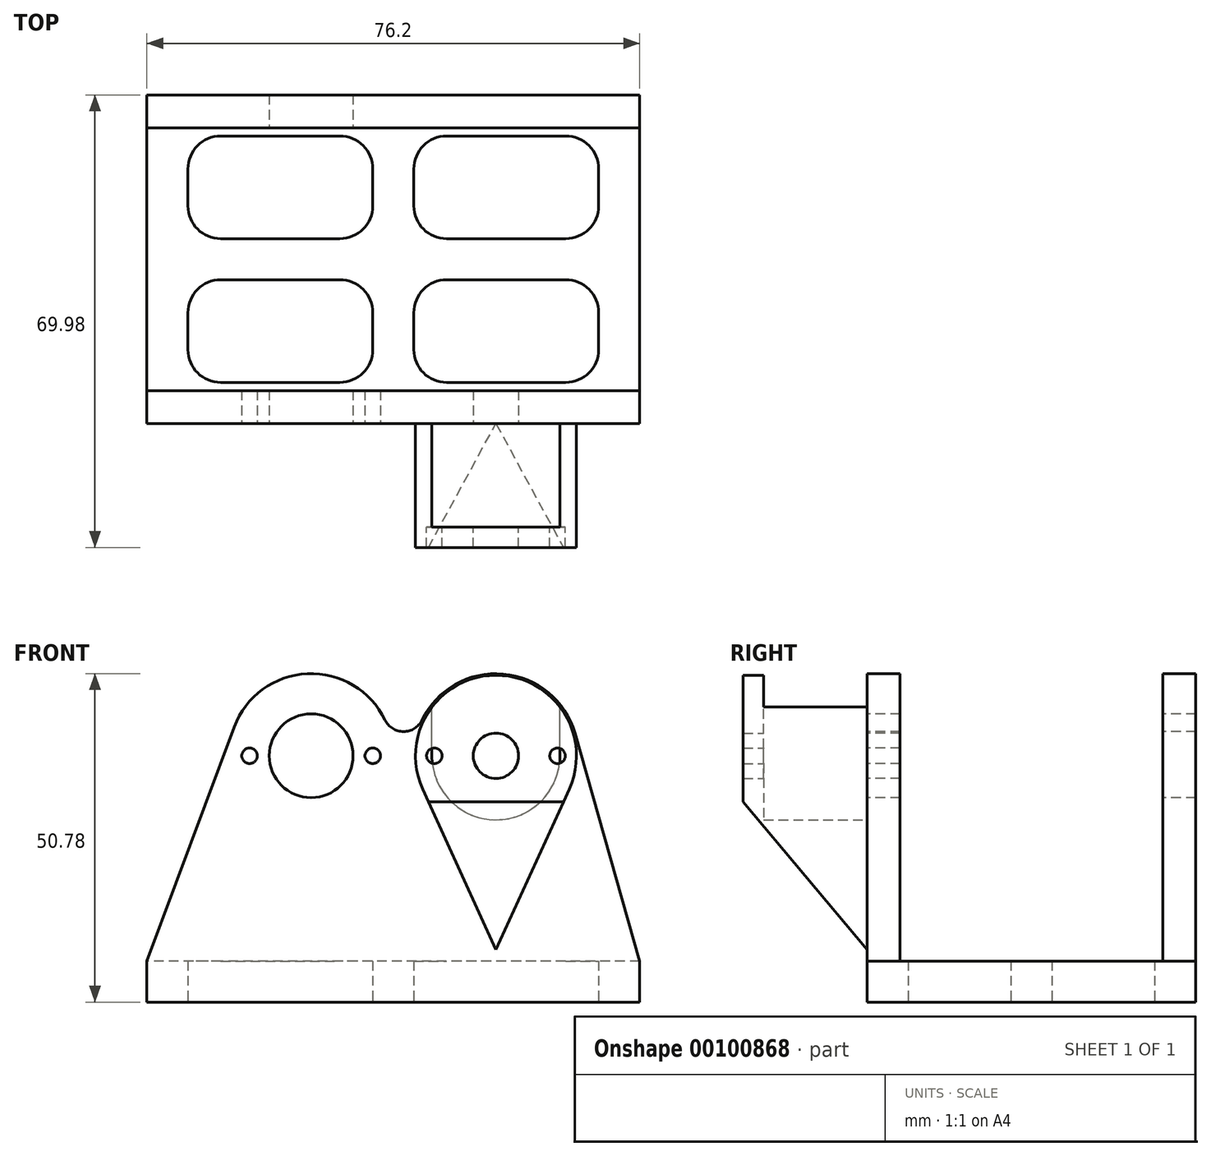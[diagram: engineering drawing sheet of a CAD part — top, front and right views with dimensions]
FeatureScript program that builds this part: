
annotation { "Feature Type Name" : "Feature", "Feature Type Description" : "" }
export const myFeature = defineFeature(function(context is Context, id is Id, definition is map)
    precondition{}
    {
        {
            var Q0;
            Q0=qCreatedBy(makeId("Top.planeOp"),FACE);
            var sketch = newSketch(context, id + "F0", { "sketchPlane" : qUnion([Q0])});
            skLineSegment(sketch, "E0.bottom", {"start": v(38.1, -25.4) * mm, "end": v(-38.1, -25.4) * mm});
            skLineSegment(sketch, "E0.top", {"start": v(38.1, 25.4) * mm, "end": v(-38.1, 25.4) * mm});
            skLineSegment(sketch, "E0.left", {"start": v(38.1, -25.4) * mm, "end": v(38.1, 25.4) * mm});
            skLineSegment(sketch, "E0.right", {"start": v(-38.1, -25.4) * mm, "end": v(-38.1, 25.4) * mm});
            skPoint(sketch, "E0.middle", {"position": v(0, 0) * mm});
            skLineSegment(sketch, "E1", {"start": v(0, 0) * mm, "end": v(12.76, 0) * mm, "construction": true});
            skLineSegment(sketch, "E2", {"start": v(0, 0) * mm, "end": v(0, 25.4) * mm, "construction": true});
            skLineSegment(sketch, "E3.MirrorCS", {"start": v(0, 0) * mm, "end": v(0, -25.4) * mm, "construction": true});
            skLineSegment(sketch, "E4.bottom", {"start": v(-26.67, 19.05) * mm, "end": v(-8.26, 19.05) * mm});
            skLineSegment(sketch, "E4.top", {"start": v(-26.67, 3.17) * mm, "end": v(-8.26, 3.17) * mm});
            skLineSegment(sketch, "E4.left", {"start": v(-31.75, 13.97) * mm, "end": v(-31.75, 8.25) * mm});
            skLineSegment(sketch, "E4.right", {"start": v(-3.18, 13.97) * mm, "end": v(-3.18, 8.25) * mm});
            skPoint(sketch, "E4.middle", {"position": v(-17.46, 11.11) * mm});
            skPoint(sketch, "E5.visualSharp", {"position": v(-31.75, 3.17) * mm});
            skArc(sketch, "E5.filletArc", {"start": v(-31.75, 8.25) * mm, "mid": v(-30.26, 4.66) * mm, "end": v(-26.67, 3.17) * mm});
            skPoint(sketch, "E6.visualSharp", {"position": v(-31.75, 19.05) * mm});
            skArc(sketch, "E6.filletArc", {"start": v(-26.67, 19.05) * mm, "mid": v(-30.26, 17.56) * mm, "end": v(-31.75, 13.97) * mm});
            skPoint(sketch, "E7.visualSharp", {"position": v(-3.18, 19.05) * mm});
            skArc(sketch, "E7.filletArc", {"start": v(-3.18, 13.97) * mm, "mid": v(-4.66, 17.56) * mm, "end": v(-8.26, 19.05) * mm});
            skPoint(sketch, "E8.visualSharp", {"position": v(-3.18, 3.17) * mm});
            skArc(sketch, "E8.filletArc", {"start": v(-8.26, 3.17) * mm, "mid": v(-4.66, 4.66) * mm, "end": v(-3.18, 8.25) * mm});
            skArc(sketch, "E9.MirrorCS", {"start": v(31.75, 8.26) * mm, "mid": v(30.26, 4.66) * mm, "end": v(26.67, 3.18) * mm});
            skLineSegment(sketch, "E10.MirrorCS", {"start": v(31.75, 13.97) * mm, "end": v(31.75, 8.26) * mm});
            skArc(sketch, "E11.MirrorCS", {"start": v(26.67, 19.05) * mm, "mid": v(30.26, 17.56) * mm, "end": v(31.75, 13.97) * mm});
            skLineSegment(sketch, "E12.MirrorCS", {"start": v(26.67, 19.05) * mm, "end": v(8.25, 19.05) * mm});
            skArc(sketch, "E13.MirrorCS", {"start": v(3.17, 13.97) * mm, "mid": v(4.66, 17.56) * mm, "end": v(8.25, 19.05) * mm});
            skLineSegment(sketch, "E14.MirrorCS", {"start": v(3.17, 13.97) * mm, "end": v(3.17, 8.25) * mm});
            skArc(sketch, "E15.MirrorCS", {"start": v(8.26, 3.18) * mm, "mid": v(4.66, 4.66) * mm, "end": v(3.17, 8.25) * mm});
            skLineSegment(sketch, "E16.MirrorCS", {"start": v(26.67, 3.18) * mm, "end": v(8.26, 3.17) * mm});
            skLineSegment(sketch, "E17.MirrorCS", {"start": v(-26.67, -3.18) * mm, "end": v(-8.26, -3.18) * mm});
            skArc(sketch, "E18.MirrorCS", {"start": v(-31.75, -8.26) * mm, "mid": v(-30.26, -4.66) * mm, "end": v(-26.67, -3.18) * mm});
            skLineSegment(sketch, "E19.MirrorCS", {"start": v(-31.75, -13.97) * mm, "end": v(-31.75, -8.26) * mm});
            skArc(sketch, "E20.MirrorCS", {"start": v(-26.67, -19.05) * mm, "mid": v(-30.26, -17.56) * mm, "end": v(-31.75, -13.97) * mm});
            skLineSegment(sketch, "E21.MirrorCS", {"start": v(-26.67, -19.05) * mm, "end": v(-8.25, -19.05) * mm});
            skArc(sketch, "E22.MirrorCS", {"start": v(-3.17, -13.97) * mm, "mid": v(-4.66, -17.56) * mm, "end": v(-8.25, -19.05) * mm});
            skLineSegment(sketch, "E23.MirrorCS", {"start": v(-3.17, -13.97) * mm, "end": v(-3.17, -8.26) * mm});
            skPoint(sketch, "E24.MirrorP", {"position": v(-3.17, -3.18) * mm});
            skArc(sketch, "E25.MirrorCS", {"start": v(-8.26, -3.18) * mm, "mid": v(-4.66, -4.66) * mm, "end": v(-3.17, -8.26) * mm});
            skLineSegment(sketch, "E26.MirrorCS", {"start": v(3.18, -13.97) * mm, "end": v(3.18, -8.26) * mm});
            skArc(sketch, "E27.MirrorCS", {"start": v(8.26, -3.17) * mm, "mid": v(4.66, -4.66) * mm, "end": v(3.18, -8.26) * mm});
            skArc(sketch, "E28.MirrorCS", {"start": v(3.18, -13.97) * mm, "mid": v(4.66, -17.56) * mm, "end": v(8.26, -19.05) * mm});
            skLineSegment(sketch, "E29.MirrorCS", {"start": v(26.67, -19.05) * mm, "end": v(8.26, -19.05) * mm});
            skLineSegment(sketch, "E30.MirrorCS", {"start": v(26.67, -3.17) * mm, "end": v(8.26, -3.18) * mm});
            skArc(sketch, "E31.MirrorCS", {"start": v(31.75, -8.26) * mm, "mid": v(30.26, -4.66) * mm, "end": v(26.67, -3.18) * mm});
            skLineSegment(sketch, "E32.MirrorCS", {"start": v(31.75, -13.97) * mm, "end": v(31.75, -8.26) * mm});
            skArc(sketch, "E33.MirrorCS", {"start": v(26.67, -19.05) * mm, "mid": v(30.26, -17.56) * mm, "end": v(31.75, -13.97) * mm});
            skSolve(sketch);
        }
        {
            var Q0;
            Q0 = qSketchRegion(id + "F0", true);
            extrude(context, id + "F1", {"entities" : qUnion([Q0]), "depth" : 6.35 * mm});
        }
        {
            var Q0;
            Q0=makeQuery(id+"F1.opExtrude","CAP_FACE",FACE,{"disambiguationData":[OSD([sQuery(id+"F0.wireOp",EDGE,"E0.bottom"),sQuery(id+"F0.wireOp",EDGE,"E0.top"),sQuery(id+"F0.wireOp",EDGE,"E0.left"),sQuery(id+"F0.wireOp",EDGE,"E0.right")])],"isStart":false});
            var sketch = newSketch(context, id + "F2", { "sketchPlane" : qUnion([Q0])});
            skLineSegment(sketch, "E34.bottom", {"start": v(-38.1, 25.4) * mm, "end": v(38.1, 25.4) * mm});
            skLineSegment(sketch, "E34.top", {"start": v(-38.1, 20.32) * mm, "end": v(38.1, 20.32) * mm});
            skLineSegment(sketch, "E34.left", {"start": v(-38.1, 25.4) * mm, "end": v(-38.1, 20.32) * mm});
            skLineSegment(sketch, "E34.right", {"start": v(38.1, 25.4) * mm, "end": v(38.1, 20.32) * mm});
            skLineSegment(sketch, "E35.bottom", {"start": v(38.1, -25.4) * mm, "end": v(-38.1, -25.4) * mm});
            skLineSegment(sketch, "E35.top", {"start": v(38.1, -20.32) * mm, "end": v(-38.1, -20.32) * mm});
            skLineSegment(sketch, "E35.left", {"start": v(38.1, -25.4) * mm, "end": v(38.1, -20.32) * mm});
            skLineSegment(sketch, "E35.right", {"start": v(-38.1, -25.4) * mm, "end": v(-38.1, -20.32) * mm});
            skSolve(sketch);
        }
        {
            var Q0;
            Q0 = qSketchRegion(id + "F2", true);
            extrude(context, id + "F3", {"entities" : qUnion([Q0]), "operationType" : NewBodyOperationType.ADD, "depth" : 101.6 * mm});
        }
        {
            var Q0;
            Q0=makeQuery(id+"F3.boolean.opBoolean","MERGE",FACE,{"derivedFrom":[makeQuery(id+"F1.opExtrude","SWEPT_FACE",FACE,{"disambiguationData":[OSD([sQuery(id+"F0.wireOp",EDGE,"E0.bottom")])]}),makeQuery(id+"F3.opExtrude","SWEPT_FACE",FACE,{"disambiguationData":[OSD([sQuery(id+"F2.wireOp",EDGE,"E35.bottom")])]})]});
            var sketch = newSketch(context, id + "F4", { "sketchPlane" : qUnion([Q0])});
            skCircle(sketch, "E36", {"center": v(-12.7, 38.08) * mm, "radius": 6.48 * mm});
            skCircle(sketch, "E37", {"center": v(-22.22, 38.08) * mm, "radius": 1.2 * mm});
            skCircle(sketch, "E38", {"center": v(-3.17, 38.08) * mm, "radius": 1.2 * mm});
            skLineSegment(sketch, "E39", {"start": v(-3.17, 38.08) * mm, "end": v(-12.7, 38.08) * mm, "construction": true});
            skLineSegment(sketch, "E40", {"start": v(-12.7, 38.08) * mm, "end": v(-22.22, 38.08) * mm, "construction": true});
            skCircle(sketch, "E41", {"center": v(-12.7, 38.08) * mm, "radius": 28.58 * mm, "construction": true});
            skPoint(sketch, "E42.visualSharp", {"position": v(19.22, 48.59) * mm});
            skPoint(sketch, "E43.visualSharp", {"position": v(-7.63, 23.99) * mm});
            skLineSegment(sketch, "E44", {"start": v(38.1, 6.35) * mm, "end": v(38.1, 107.95) * mm});
            skLineSegment(sketch, "E45", {"start": v(38.1, 107.95) * mm, "end": v(-38.1, 107.95) * mm});
            skLineSegment(sketch, "E46", {"start": v(-38.1, 107.95) * mm, "end": v(-38.1, 6.35) * mm});
            skArc(sketch, "E47", {"start": v(-1.27, 43.62) * mm, "mid": v(-13.3, 50.77) * mm, "end": v(-24.6, 42.52) * mm});
            skLineSegment(sketch, "E48", {"start": v(-38.1, 6.35) * mm, "end": v(-24.6, 42.52) * mm});
            skLineSegment(sketch, "E49", {"start": v(38.1, 6.35) * mm, "end": v(28.1, 41.55) * mm});
            skPoint(sketch, "E50.center.orphan", {"position": v(15.88, 38.08) * mm});
            skPoint(sketch, "E51.visualSharp", {"position": v(-1.27, 32.55) * mm});
            skPoint(sketch, "E52.visualSharp", {"position": v(31.24, 47.34) * mm});
            skPoint(sketch, "E53.visualSharp", {"position": v(-1.27, 43.62) * mm});
            skPoint(sketch, "E54.visualSharp", {"position": v(33.41, 33.23) * mm});
            skCircle(sketch, "E55", {"center": v(15.88, 38.08) * mm, "radius": 3.5 * mm});
            skArc(sketch, "E56", {"start": v(28.1, 41.55) * mm, "mid": v(16.98, 50.73) * mm, "end": v(4.45, 43.62) * mm});
            skArc(sketch, "E57", {"start": v(-1.27, 43.62) * mm, "mid": v(1.59, 41.83) * mm, "end": v(4.45, 43.62) * mm});
            skSolve(sketch);
        }
        {
            var Q0;
            Q0=makeQuery(id+"F4.imprint","IMPRINT",FACE,{"disambiguationData":[TD([[makeQuery(id+"F4.imprint","IMPRINT",EDGE,{"derivedFrom":sQuery(id+"F4.wireOp",EDGE,"E44")}),-1.0]])]});
            var Q1;
            Q1=makeQuery(id+"F4.imprint","IMPRINT",FACE,{"disambiguationData":[TD([[makeQuery(id+"F4.imprint","IMPRINT",EDGE,{"derivedFrom":sQuery(id+"F4.wireOp",EDGE,"VKw5fcWm-w3NF-tdAb-OPDk-Neu4bGwbLTaV")}),1.0]])]});
            var Q2;
            Q2=makeQuery(id+"F4.imprint","IMPRINT",FACE,{"disambiguationData":[TD([[makeQuery(id+"F4.imprint","IMPRINT",EDGE,{"derivedFrom":sQuery(id+"F4.wireOp",EDGE,"E36")}),1.0]])]});
            extrude(context, id + "F5", {"entities" : qUnion([Q0, Q1, Q2]), "operationType" : NewBodyOperationType.REMOVE, "endBound" : BoundingType.THROUGH_ALL, "oppositeDirection" : true, "depth" : 25.4 * mm});
        }
        {
            var Q0;
            Q0=makeQuery(id+"F4.imprint","IMPRINT",FACE,{"disambiguationData":[TD([[makeQuery(id+"F4.imprint","IMPRINT",EDGE,{"derivedFrom":sQuery(id+"F4.wireOp",EDGE,"E38")}),1.0]])]});
            var Q1;
            Q1=makeQuery(id+"F4.imprint","IMPRINT",FACE,{"disambiguationData":[TD([[makeQuery(id+"F4.imprint","IMPRINT",EDGE,{"derivedFrom":sQuery(id+"F4.wireOp",EDGE,"E37")}),1.0]])]});
            var Q2;
            Q2=makeQuery(id+"F4.imprint","IMPRINT",FACE,{"disambiguationData":[TD([[makeQuery(id+"F4.imprint","IMPRINT",EDGE,{"derivedFrom":sQuery(id+"F4.wireOp",EDGE,"E55")}),1.0]])]});
            var Q3;
            Q3=makeQuery(id+"F3.opExtrude","SWEPT_FACE",FACE,{"disambiguationData":[OSD([sQuery(id+"F2.wireOp",EDGE,"E35.top")])]});
            extrude(context, id + "F6", {"entities" : qUnion([Q0, Q1, Q2]), "operationType" : NewBodyOperationType.REMOVE, "endBound" : BoundingType.UP_TO_SURFACE, "oppositeDirection" : true, "endBoundEntityFace" : qUnion([Q3]), "depth" : 25.4 * mm});
        }
        {
            var Q0;
            Q0=makeQuery(id+"F4.imprint","IMPRINT",FACE,{"disambiguationData":[TD([[makeQuery(id+"F4.imprint","IMPRINT",EDGE,{"derivedFrom":sQuery(id+"F4.wireOp",EDGE,"E36")}),-1.0]])]});
            var sketch = newSketch(context, id + "F7", { "sketchPlane" : qUnion([Q0])});
            skArc(sketch, "E58", {"start": v(5.97, 38.08) * mm, "mid": v(15.88, 28.18) * mm, "end": v(25.78, 38.08) * mm});
            skArc(sketch, "E59", {"start": v(5.97, 45.62) * mm, "mid": v(15.88, 25.64) * mm, "end": v(25.78, 45.62) * mm});
            skLineSegment(sketch, "E60", {"start": v(25.78, 38.08) * mm, "end": v(25.78, 45.62) * mm});
            skLineSegment(sketch, "E61", {"start": v(5.97, 38.08) * mm, "end": v(5.97, 45.62) * mm});
            skSolve(sketch);
        }
        {
            var Q0;
            Q0 = qSketchRegion(id + "F7", true);
            extrude(context, id + "F8", {"entities" : qUnion([Q0]), "operationType" : NewBodyOperationType.ADD, "depth" : 16 * mm});
        }
        {
            var Q0;
            Q0=makeQuery(id+"F8.opExtrude","CAP_FACE",FACE,{"disambiguationData":[OSD([sQuery(id+"F7.wireOp",EDGE,"E58"),sQuery(id+"F7.wireOp",EDGE,"E59"),sQuery(id+"F7.wireOp",EDGE,"E60"),sQuery(id+"F7.wireOp",EDGE,"E61")])],"isStart":false});
            var sketch = newSketch(context, id + "F9", { "sketchPlane" : qUnion([Q0])});
            skCircle(sketch, "E62", {"center": v(15.88, 38.08) * mm, "radius": 12.45 * mm});
            skCircle(sketch, "E63", {"center": v(15.88, 38.08) * mm, "radius": 3.5 * mm});
            skLineSegment(sketch, "E64", {"start": v(25.4, 38.08) * mm, "end": v(6.35, 38.08) * mm, "construction": true});
            skCircle(sketch, "E65", {"center": v(25.4, 38.08) * mm, "radius": 1.2 * mm});
            skCircle(sketch, "E66", {"center": v(6.35, 38.08) * mm, "radius": 1.2 * mm});
            skSolve(sketch);
        }
        {
            var Q0;
            Q0 = qSketchRegion(id + "F9", true);
            var Q1;
            Q1 = qConstructionFilter(qBodyType(qCreatedBy(id + "F9" ,EDGE), BodyType.WIRE), ConstructionObject.NO);
            extrude(context, id + "F10", {"entities" : qUnion([Q0]), "operationType" : NewBodyOperationType.ADD, "surfaceEntities" : qUnion([Q1]), "depth" : 3.17 * mm});
        }
        {
            var Q0;
            Q0=makeQuery(id+"F4.imprint","IMPRINT",FACE,{"disambiguationData":[TD([[makeQuery(id+"F4.imprint","IMPRINT",EDGE,{"derivedFrom":sQuery(id+"F4.wireOp",EDGE,"E36")}),-1.0]])]});
            var sketch = newSketch(context, id + "F11", { "sketchPlane" : qUnion([Q0])});
            skLineSegment(sketch, "E67", {"start": v(15.88, 8.13) * mm, "end": v(27.2, 32.91) * mm});
            skLineSegment(sketch, "E68", {"start": v(4.55, 32.91) * mm, "end": v(15.88, 8.13) * mm});
            skArc(sketch, "E69", {"start": v(4.55, 32.91) * mm, "mid": v(15.88, 25.64) * mm, "end": v(27.2, 32.91) * mm});
            skLineSegment(sketch, "E70", {"start": v(15.88, 8.13) * mm, "end": v(15.88, 29.15) * mm, "construction": true});
            skSolve(sketch);
        }
        {
            var Q0;
            Q0 = qSketchRegion(id + "F11", true);
            var Q1;
            Q1=makeQuery(id+"F10.opExtrude","CAP_FACE",FACE,{"disambiguationData":[OSD([sQuery(id+"F9.wireOp",EDGE,"E62"),sQuery(id+"F9.wireOp",EDGE,"E63"),sQuery(id+"F9.wireOp",EDGE,"E65"),sQuery(id+"F9.wireOp",EDGE,"E66")])],"isStart":false});
            extrude(context, id + "F12", {"entities" : qUnion([Q0]), "operationType" : NewBodyOperationType.ADD, "endBound" : BoundingType.UP_TO_SURFACE, "endBoundEntityFace" : qUnion([Q1]), "depth" : 25.4 * mm});
        }
        {
            var Q0;
            Q0=qCreatedBy(makeId("Right.planeOp"),FACE);
            var sketch = newSketch(context, id + "F13", { "sketchPlane" : qUnion([Q0])});
            skLineSegment(sketch, "E71", {"start": v(-44.58, 30.98) * mm, "end": v(-25.4, 8.13) * mm});
            skLineSegment(sketch, "E72", {"start": v(-25.4, 8.13) * mm, "end": v(-44.58, 8.13) * mm});
            skLineSegment(sketch, "E73", {"start": v(-44.58, 8.13) * mm, "end": v(-44.58, 30.98) * mm});
            skSolve(sketch);
        }
        {
            var Q0;
            Q0 = qSketchRegion(id + "F13", true);
            extrude(context, id + "F14", {"entities" : qUnion([Q0]), "operationType" : NewBodyOperationType.REMOVE, "endBound" : BoundingType.THROUGH_ALL, "oppositeDirection" : true, "depth" : 25.4 * mm, "hasSecondDirection" : true, "secondDirectionBound" : BoundingType.THROUGH_ALL, "secondDirectionOppositeDirection" : false, "secondDirectionDepth" : 25.4 * mm});
        }
    });
